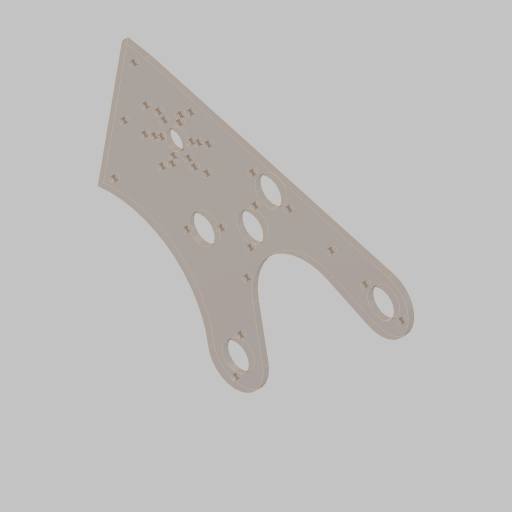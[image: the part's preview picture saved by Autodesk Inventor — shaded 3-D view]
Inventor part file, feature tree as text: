
AUTODESK INVENTOR PART (.ipt)
format: ipt  version: 2023.5 (Build 275446000, 446)  size: 269,312 bytes
history: native  units: in
note: dims shown in document units (in); Inventor stores cm internally (conversion verified against a paired STEP export)
features: sketch x2, hole x2, extrude x1, projected_geometry x1
ambient origin geometry x8: Origin, YZ Plane, XZ Plane, XY Plane, X Axis, Y Axis, Z Axis, Center Point
bodies: Solid1 (feature_tree)
feature tree (6):
  sketch  "Sketch1"  dims[d3=0.3489in d4=0.0in]
  extrude  "Extrusion1"  TaperAngle=0.0deg  [1 undecoded]
  hole  "Hole1"  [1 undecoded]
  hole  "Hole2"  [1 undecoded]
  sketch  "Sketch2"  dims[d7=4.0in d8=4.0in d9=1.123in d10=4.0in d11=4.5in d12=4.5in d13=0.625in d14=0.625in d15=5.113in d16=1.125in d17=5.113in d18=1.8765in d19=1.8765in d22=1.0in d23=6.0in d26=10.0585in d27=2.5in d30=8.0in d31=0.0687in d32=0.75in d33=4.75in d34=1.375in d35=0.75in d36=0.25in d38=2.3622in d40=360.0deg d44=0.375in d45=0.25in d46=0.0in d47=0.201in d48=0.75in d49=0.37in d50=0.25in d51=90.0deg d52=1.0in d53=0.8108in d55=0.5497in d56=0.3in d58=2.256in d59=2.5in d60=2.9555in d61=2.35in d62=0.3779in d65=2.0in d66=2.3622in d68=360.0deg d70=1.625in d71=60.0deg d72=1.655in d73=0.201in d74=0.75in d75=0.385in d76=0.25in d77=0.5635in d78=1.0in d79=0.8108in d80=1.5748in d82=360.0deg d85=1.5748in d87=360.0deg d89=45.0deg d90=0.25in d91=0.825in d92=4.25in]
  projected_geometry  "Projected Loop1"
note: 3 required parameter values undecoded (feature->parameter linkage not recoverable at this tier; creation-order binding heuristic only, values carry confidence <= 0.55)
